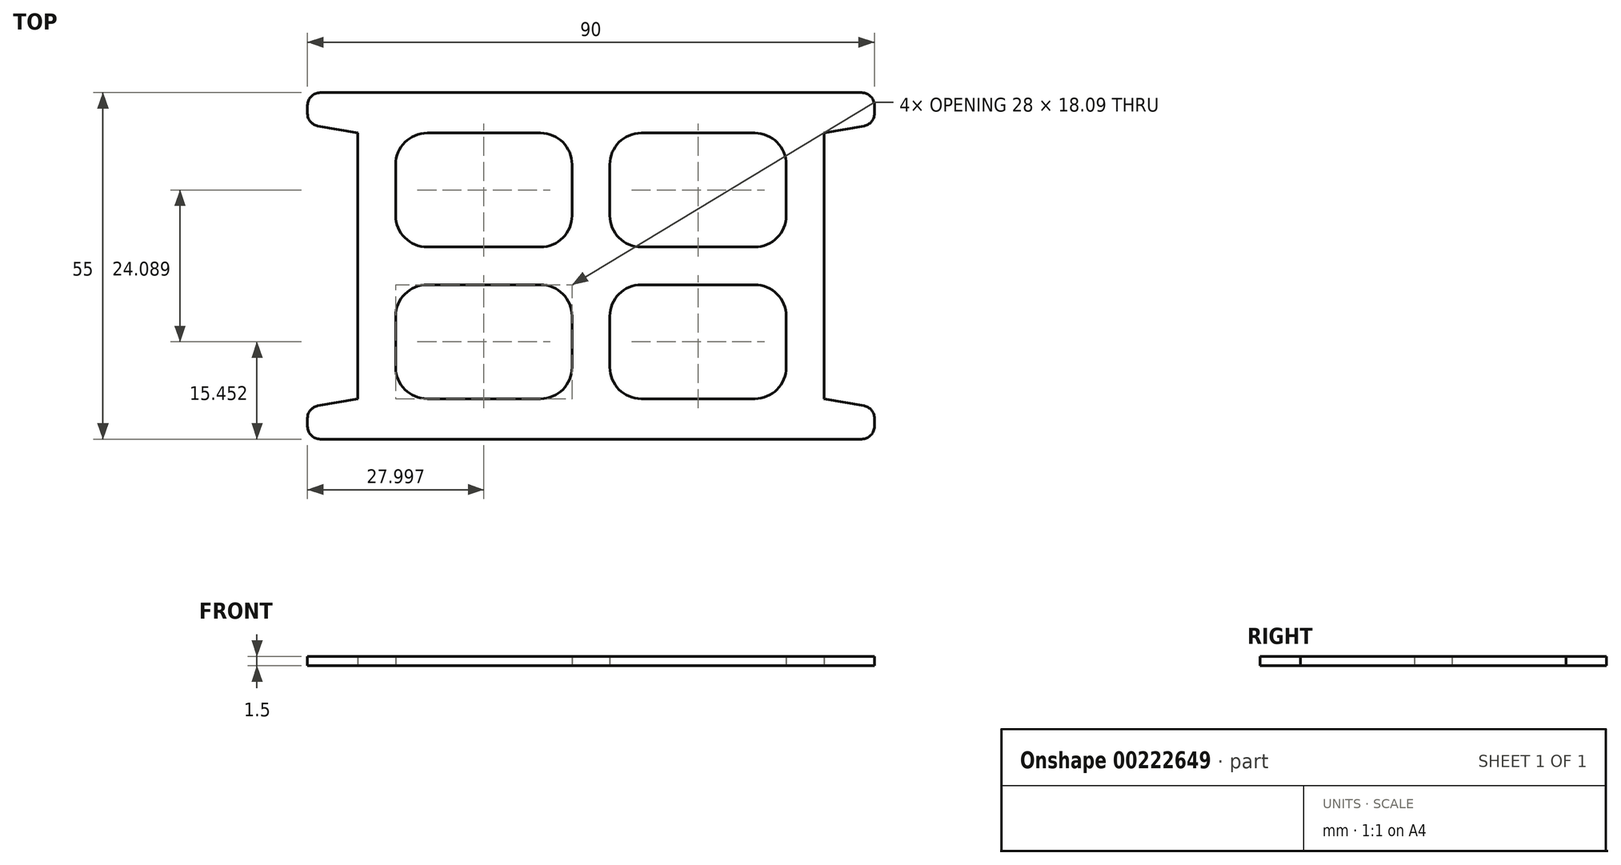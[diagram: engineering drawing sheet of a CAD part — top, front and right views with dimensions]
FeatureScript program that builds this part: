
annotation { "Feature Type Name" : "Feature", "Feature Type Description" : "" }
export const myFeature = defineFeature(function(context is Context, id is Id, definition is map)
    precondition{}
    {
        {
            var Q0;
            Q0=qCreatedBy(makeId("Top.planeOp"),FACE);
            var sketch = newSketch(context, id + "F0", { "sketchPlane" : qUnion([Q0])});
            skLineSegment(sketch, "E0.bottom", {"start": v(-32, 17.59) * mm, "end": v(58, 17.59) * mm});
            skLineSegment(sketch, "E0.top", {"start": v(-32, -37.41) * mm, "end": v(58, -37.41) * mm});
            skLineSegment(sketch, "E0.left", {"start": v(-32, 17.59) * mm, "end": v(-32, -37.41) * mm});
            skLineSegment(sketch, "E0.right", {"start": v(58, 17.59) * mm, "end": v(58, -37.41) * mm});
            skLineSegment(sketch, "E1", {"start": v(13, 17.59) * mm, "end": v(13, -37.41) * mm, "construction": true});
            skLineSegment(sketch, "E2", {"start": v(58, -9.91) * mm, "end": v(-32, -9.91) * mm, "construction": true});
            skLineSegment(sketch, "E3", {"start": v(-32, 12.59) * mm, "end": v(-24, 11.18) * mm});
            skLineSegment(sketch, "E4", {"start": v(-24, 11.18) * mm, "end": v(-24, -9.91) * mm});
            skLineSegment(sketch, "E5.MirrorCS", {"start": v(58, 12.59) * mm, "end": v(50, 11.18) * mm});
            skLineSegment(sketch, "E6.MirrorCS", {"start": v(50, 11.18) * mm, "end": v(50, -9.91) * mm});
            skLineSegment(sketch, "E7.MirrorCS", {"start": v(-24, -31) * mm, "end": v(-24, -9.91) * mm});
            skLineSegment(sketch, "E8.MirrorCS", {"start": v(-32, -32.41) * mm, "end": v(-24, -31) * mm});
            skLineSegment(sketch, "E9.MirrorCS", {"start": v(50, -31) * mm, "end": v(50, -9.91) * mm});
            skLineSegment(sketch, "E10.MirrorCS", {"start": v(58, -32.41) * mm, "end": v(50, -31) * mm});
            skLineSegment(sketch, "E11.bottom", {"start": v(-18, 11.18) * mm, "end": v(10, 11.18) * mm});
            skLineSegment(sketch, "E11.top", {"start": v(-18, -6.91) * mm, "end": v(10, -6.91) * mm});
            skLineSegment(sketch, "E11.left", {"start": v(-18, 11.18) * mm, "end": v(-18, -6.91) * mm});
            skLineSegment(sketch, "E11.right", {"start": v(10, 11.18) * mm, "end": v(10, -6.91) * mm});
            skLineSegment(sketch, "E12.MirrorCS", {"start": v(16, 11.18) * mm, "end": v(16, -6.91) * mm});
            skLineSegment(sketch, "E13.MirrorCS", {"start": v(44, 11.18) * mm, "end": v(16, 11.18) * mm});
            skLineSegment(sketch, "E14.MirrorCS", {"start": v(44, 11.18) * mm, "end": v(44, -6.91) * mm});
            skLineSegment(sketch, "E15.MirrorCS", {"start": v(44, -6.91) * mm, "end": v(16, -6.91) * mm});
            skLineSegment(sketch, "E16.MirrorCS", {"start": v(-18, -31) * mm, "end": v(-18, -12.91) * mm});
            skLineSegment(sketch, "E17.MirrorCS", {"start": v(10, -31) * mm, "end": v(10, -12.91) * mm});
            skLineSegment(sketch, "E18.MirrorCS", {"start": v(-18, -31) * mm, "end": v(10, -31) * mm});
            skLineSegment(sketch, "E19.MirrorCS", {"start": v(-18, -12.91) * mm, "end": v(10, -12.91) * mm});
            skLineSegment(sketch, "E20.MirrorCS", {"start": v(16, -31) * mm, "end": v(16, -12.91) * mm});
            skLineSegment(sketch, "E21.MirrorCS", {"start": v(44, -31) * mm, "end": v(44, -12.91) * mm});
            skLineSegment(sketch, "E22.MirrorCS", {"start": v(44, -12.91) * mm, "end": v(16, -12.91) * mm});
            skLineSegment(sketch, "E23.MirrorCS", {"start": v(44, -31) * mm, "end": v(16, -31) * mm});
            skSolve(sketch);
        }
        {
            var Q0;
            {var subQ3=sQuery(id+"F0.wireOp",EDGE,"E0.bottom");Q0=makeQuery(id+"F0.imprint","IMPRINT",FACE,{"disambiguationData":[TD([[makeQuery(id+"F0.imprint","IMPRINT",EDGE,{"derivedFrom":subQ3}),-1.0]])]});}
            extrude(context, id + "F1", {"entities" : qUnion([Q0]), "depth" : 1.5 * mm});
        }
        {
            var Q0;
            Q0=makeQuery(id+"F1.opExtrude","SWEPT_EDGE",EDGE,{"disambiguationData":[OSD([sQuery(id+"F0.wireOp",EDGE,"E13.MirrorCS"),sQuery(id+"F0.wireOp",EDGE,"E14.MirrorCS")])]});
            var Q1;
            Q1=makeQuery(id+"F1.opExtrude","SWEPT_EDGE",EDGE,{"disambiguationData":[OSD([sQuery(id+"F0.wireOp",EDGE,"E11.bottom"),sQuery(id+"F0.wireOp",EDGE,"E11.right")])]});
            var Q2;
            Q2=makeQuery(id+"F1.opExtrude","SWEPT_EDGE",EDGE,{"disambiguationData":[OSD([sQuery(id+"F0.wireOp",EDGE,"E21.MirrorCS"),sQuery(id+"F0.wireOp",EDGE,"E22.MirrorCS")])]});
            var Q3;
            Q3=makeQuery(id+"F1.opExtrude","SWEPT_EDGE",EDGE,{"disambiguationData":[OSD([sQuery(id+"F0.wireOp",EDGE,"E17.MirrorCS"),sQuery(id+"F0.wireOp",EDGE,"E19.MirrorCS")])]});
            var Q4;
            Q4=makeQuery(id+"F1.opExtrude","SWEPT_EDGE",EDGE,{"disambiguationData":[OSD([sQuery(id+"F0.wireOp",EDGE,"E12.MirrorCS"),sQuery(id+"F0.wireOp",EDGE,"E13.MirrorCS")])]});
            var Q5;
            Q5=makeQuery(id+"F1.opExtrude","SWEPT_EDGE",EDGE,{"disambiguationData":[OSD([sQuery(id+"F0.wireOp",EDGE,"E11.bottom"),sQuery(id+"F0.wireOp",EDGE,"E11.left")])]});
            var Q6;
            Q6=makeQuery(id+"F1.opExtrude","SWEPT_EDGE",EDGE,{"disambiguationData":[OSD([sQuery(id+"F0.wireOp",EDGE,"E16.MirrorCS"),sQuery(id+"F0.wireOp",EDGE,"E19.MirrorCS")])]});
            var Q7;
            Q7=makeQuery(id+"F1.opExtrude","SWEPT_EDGE",EDGE,{"disambiguationData":[OSD([sQuery(id+"F0.wireOp",EDGE,"E20.MirrorCS"),sQuery(id+"F0.wireOp",EDGE,"E22.MirrorCS")])]});
            var Q8;
            Q8=makeQuery(id+"F1.opExtrude","SWEPT_EDGE",EDGE,{"disambiguationData":[OSD([sQuery(id+"F0.wireOp",EDGE,"E12.MirrorCS"),sQuery(id+"F0.wireOp",EDGE,"E15.MirrorCS")])]});
            var Q9;
            Q9=makeQuery(id+"F1.opExtrude","SWEPT_EDGE",EDGE,{"disambiguationData":[OSD([sQuery(id+"F0.wireOp",EDGE,"E11.top"),sQuery(id+"F0.wireOp",EDGE,"E11.left")])]});
            var Q10;
            Q10=makeQuery(id+"F1.opExtrude","SWEPT_EDGE",EDGE,{"disambiguationData":[OSD([sQuery(id+"F0.wireOp",EDGE,"E16.MirrorCS"),sQuery(id+"F0.wireOp",EDGE,"E18.MirrorCS")])]});
            var Q11;
            Q11=makeQuery(id+"F1.opExtrude","SWEPT_EDGE",EDGE,{"disambiguationData":[OSD([sQuery(id+"F0.wireOp",EDGE,"E20.MirrorCS"),sQuery(id+"F0.wireOp",EDGE,"E23.MirrorCS")])]});
            var Q12;
            Q12=makeQuery(id+"F1.opExtrude","SWEPT_EDGE",EDGE,{"disambiguationData":[OSD([sQuery(id+"F0.wireOp",EDGE,"E14.MirrorCS"),sQuery(id+"F0.wireOp",EDGE,"E15.MirrorCS")])]});
            var Q13;
            Q13=makeQuery(id+"F1.opExtrude","SWEPT_EDGE",EDGE,{"disambiguationData":[OSD([sQuery(id+"F0.wireOp",EDGE,"E11.top"),sQuery(id+"F0.wireOp",EDGE,"E11.right")])]});
            var Q14;
            Q14=makeQuery(id+"F1.opExtrude","SWEPT_EDGE",EDGE,{"disambiguationData":[OSD([sQuery(id+"F0.wireOp",EDGE,"E21.MirrorCS"),sQuery(id+"F0.wireOp",EDGE,"E23.MirrorCS")])]});
            var Q15;
            Q15=makeQuery(id+"F1.opExtrude","SWEPT_EDGE",EDGE,{"disambiguationData":[OSD([sQuery(id+"F0.wireOp",EDGE,"E17.MirrorCS"),sQuery(id+"F0.wireOp",EDGE,"E18.MirrorCS")])]});
            fillet(context, id + "F2", {"entities" : qUnion([Q0, Q1, Q2, Q3, Q4, Q5, Q6, Q7, Q8, Q9, Q10, Q11, Q12, Q13, Q14, Q15]), "radius" : 5 * mm, "tangentPropagation" : true, "allowEdgeOverflow" : false});
        }
        {
            var Q0;
            Q0=makeQuery(id+"F1.opExtrude","SWEPT_EDGE",EDGE,{"disambiguationData":[OSD([sQuery(id+"F0.wireOp",EDGE,"E0.left"),sQuery(id+"F0.wireOp",EDGE,"E3")])]});
            var Q1;
            Q1=makeQuery(id+"F1.opExtrude","SWEPT_EDGE",EDGE,{"disambiguationData":[OSD([sQuery(id+"F0.wireOp",EDGE,"E0.left"),sQuery(id+"F0.wireOp",EDGE,"E8.MirrorCS")])]});
            var Q2;
            Q2=makeQuery(id+"F1.opExtrude","SWEPT_EDGE",EDGE,{"disambiguationData":[OSD([sQuery(id+"F0.wireOp",EDGE,"E0.right"),sQuery(id+"F0.wireOp",EDGE,"E5.MirrorCS")])]});
            var Q3;
            Q3=makeQuery(id+"F1.opExtrude","SWEPT_EDGE",EDGE,{"disambiguationData":[OSD([sQuery(id+"F0.wireOp",EDGE,"E0.right"),sQuery(id+"F0.wireOp",EDGE,"E10.MirrorCS")])]});
            var Q4;
            Q4=makeQuery(id+"F1.opExtrude","SWEPT_EDGE",EDGE,{"disambiguationData":[OSD([sQuery(id+"F0.wireOp",EDGE,"E0.bottom"),sQuery(id+"F0.wireOp",EDGE,"E0.right")])]});
            var Q5;
            Q5=makeQuery(id+"F1.opExtrude","SWEPT_EDGE",EDGE,{"disambiguationData":[OSD([sQuery(id+"F0.wireOp",EDGE,"E0.top"),sQuery(id+"F0.wireOp",EDGE,"E0.right")])]});
            var Q6;
            Q6=makeQuery(id+"F1.opExtrude","SWEPT_EDGE",EDGE,{"disambiguationData":[OSD([sQuery(id+"F0.wireOp",EDGE,"E0.top"),sQuery(id+"F0.wireOp",EDGE,"E0.left")])]});
            var Q7;
            Q7=makeQuery(id+"F1.opExtrude","SWEPT_EDGE",EDGE,{"disambiguationData":[OSD([sQuery(id+"F0.wireOp",EDGE,"E0.bottom"),sQuery(id+"F0.wireOp",EDGE,"E0.left")])]});
            fillet(context, id + "F3", {"entities" : qUnion([Q0, Q1, Q2, Q3, Q4, Q5, Q6, Q7]), "radius" : 2 * mm, "tangentPropagation" : true, "allowEdgeOverflow" : false});
        }
    });
